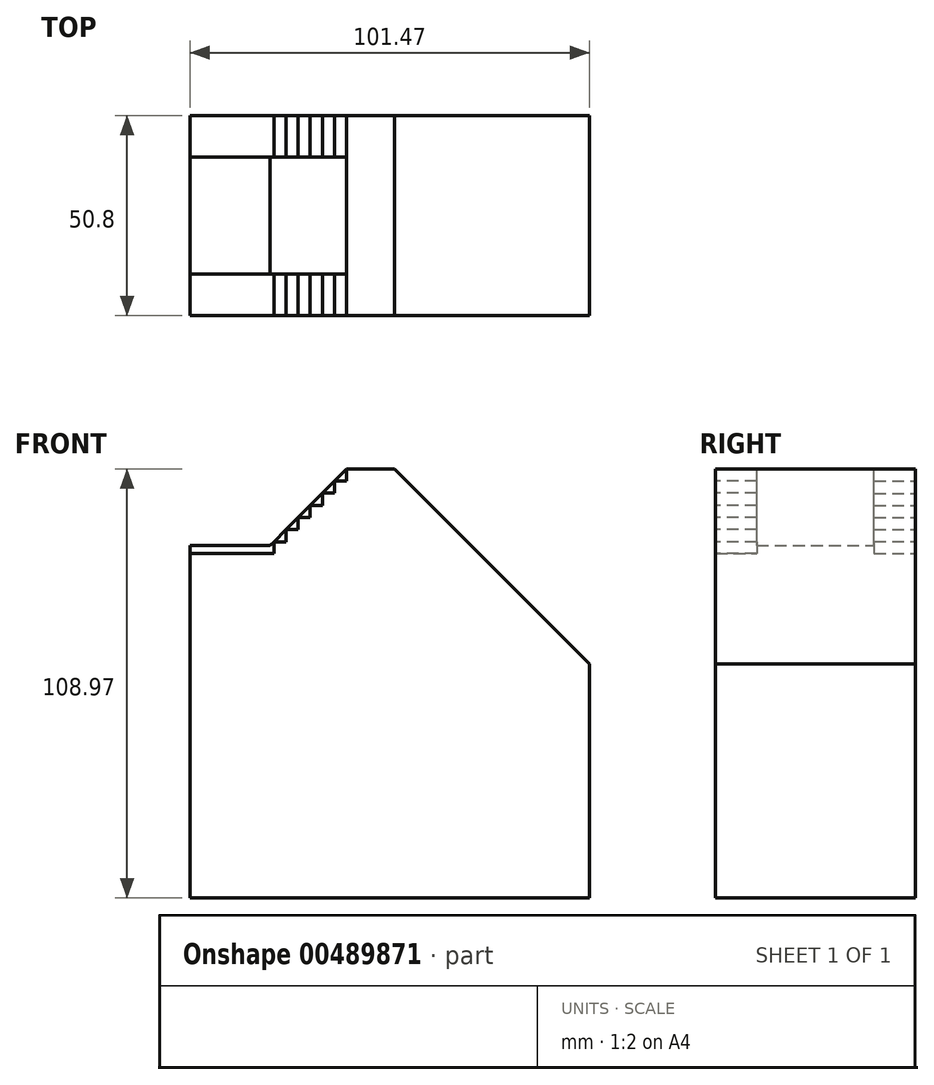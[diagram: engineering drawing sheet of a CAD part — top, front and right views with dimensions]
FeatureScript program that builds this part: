
annotation { "Feature Type Name" : "Feature", "Feature Type Description" : "" }
export const myFeature = defineFeature(function(context is Context, id is Id, definition is map)
    precondition{}
    {
        {
            var Q0;
            Q0=qCreatedBy(makeId("Front.planeOp"),FACE);
            var sketch = newSketch(context, id + "F0", { "sketchPlane" : qUnion([Q0])});
            skLineSegment(sketch, "E0", {"start": v(0, 0) * mm, "end": v(0, 87.48) * mm});
            skLineSegment(sketch, "E1", {"start": v(0, 87.48) * mm, "end": v(18.26, 87.48) * mm});
            skLineSegment(sketch, "E2", {"start": v(18.26, 87.48) * mm, "end": v(39.75, 108.97) * mm});
            skLineSegment(sketch, "E3", {"start": v(39.75, 108.97) * mm, "end": v(52, 108.97) * mm});
            skLineSegment(sketch, "E4", {"start": v(52, 108.97) * mm, "end": v(101.47, 59.49) * mm});
            skLineSegment(sketch, "E5", {"start": v(101.47, 59.49) * mm, "end": v(101.47, 0) * mm});
            skLineSegment(sketch, "E6", {"start": v(101.47, 0) * mm, "end": v(0, 0) * mm});
            skSolve(sketch);
        }
        {
            var Q0;
            Q0 = qSketchRegion(id + "F0", true);
            extrude(context, id + "F1", {"entities" : qUnion([Q0]), "depth" : 50.8 * mm});
        }
        {
            var Q0;
            Q0=makeQuery(id+"F1.opExtrude","CAP_FACE",FACE,{"disambiguationData":[OSD([sQuery(id+"F0.wireOp",EDGE,"E0"),sQuery(id+"F0.wireOp",EDGE,"E1"),sQuery(id+"F0.wireOp",EDGE,"E2"),sQuery(id+"F0.wireOp",EDGE,"E3"),sQuery(id+"F0.wireOp",EDGE,"E4"),sQuery(id+"F0.wireOp",EDGE,"E5"),sQuery(id+"F0.wireOp",EDGE,"E6")])],"isStart":false});
            var sketch = newSketch(context, id + "F2", { "sketchPlane" : qUnion([Q0])});
            skLineSegment(sketch, "E7", {"start": v(39.75, 108.97) * mm, "end": v(39.75, 105.9) * mm});
            skLineSegment(sketch, "E8", {"start": v(39.75, 105.9) * mm, "end": v(36.68, 105.9) * mm});
            skLineSegment(sketch, "E9", {"start": v(36.68, 105.9) * mm, "end": v(36.68, 102.82) * mm});
            skLineSegment(sketch, "E10", {"start": v(36.68, 102.82) * mm, "end": v(33.6, 102.82) * mm});
            skLineSegment(sketch, "E11", {"start": v(33.6, 102.82) * mm, "end": v(33.6, 99.74) * mm});
            skLineSegment(sketch, "E12", {"start": v(33.6, 99.74) * mm, "end": v(30.52, 99.74) * mm});
            skLineSegment(sketch, "E13", {"start": v(30.52, 99.74) * mm, "end": v(30.52, 96.66) * mm});
            skLineSegment(sketch, "E14", {"start": v(30.52, 96.66) * mm, "end": v(27.44, 96.66) * mm});
            skLineSegment(sketch, "E15", {"start": v(27.44, 96.66) * mm, "end": v(27.44, 93.58) * mm});
            skLineSegment(sketch, "E16", {"start": v(27.44, 93.58) * mm, "end": v(24.36, 93.58) * mm});
            skLineSegment(sketch, "E17", {"start": v(24.36, 93.58) * mm, "end": v(24.36, 90.5) * mm});
            skLineSegment(sketch, "E18", {"start": v(24.36, 90.5) * mm, "end": v(21.28, 90.5) * mm});
            skLineSegment(sketch, "E19", {"start": v(21.28, 90.5) * mm, "end": v(21.28, 87.48) * mm});
            skLineSegment(sketch, "E20", {"start": v(21.28, 87.48) * mm, "end": v(18.26, 87.48) * mm});
            skLineSegment(sketch, "E21", {"start": v(18.26, 87.48) * mm, "end": v(39.75, 108.97) * mm});
            skSolve(sketch);
        }
        {
            var Q0;
            Q0 = qSketchRegion(id + "F2", true);
            extrude(context, id + "F3", {"entities" : qUnion([Q0]), "operationType" : NewBodyOperationType.REMOVE, "oppositeDirection" : true, "depth" : 10.5 * mm});
        }
        {
            var Q0;
            Q0=makeQuery(id+"F1.opExtrude","CAP_FACE",FACE,{"disambiguationData":[OSD([sQuery(id+"F0.wireOp",EDGE,"E0"),sQuery(id+"F0.wireOp",EDGE,"E1"),sQuery(id+"F0.wireOp",EDGE,"E2"),sQuery(id+"F0.wireOp",EDGE,"E3"),sQuery(id+"F0.wireOp",EDGE,"E4"),sQuery(id+"F0.wireOp",EDGE,"E5"),sQuery(id+"F0.wireOp",EDGE,"E6")])],"isStart":true});
            var sketch = newSketch(context, id + "F4", { "sketchPlane" : qUnion([Q0])});
            skLineSegment(sketch, "E22", {"start": v(-39.75, 108.97) * mm, "end": v(-39.75, 105.9) * mm});
            skLineSegment(sketch, "E23", {"start": v(-39.75, 105.9) * mm, "end": v(-36.67, 105.9) * mm});
            skLineSegment(sketch, "E24", {"start": v(-36.67, 105.9) * mm, "end": v(-36.67, 102.81) * mm});
            skLineSegment(sketch, "E25", {"start": v(-36.67, 102.81) * mm, "end": v(-33.6, 102.81) * mm});
            skLineSegment(sketch, "E26", {"start": v(-33.6, 102.81) * mm, "end": v(-33.6, 99.74) * mm});
            skLineSegment(sketch, "E27", {"start": v(-33.6, 99.74) * mm, "end": v(-30.52, 99.74) * mm});
            skLineSegment(sketch, "E28", {"start": v(-30.52, 99.74) * mm, "end": v(-30.52, 96.66) * mm});
            skLineSegment(sketch, "E29", {"start": v(-30.52, 96.66) * mm, "end": v(-27.44, 96.66) * mm});
            skLineSegment(sketch, "E30", {"start": v(-27.44, 96.66) * mm, "end": v(-27.44, 93.58) * mm});
            skLineSegment(sketch, "E31", {"start": v(-27.44, 93.58) * mm, "end": v(-24.36, 93.58) * mm});
            skLineSegment(sketch, "E32", {"start": v(-24.36, 93.58) * mm, "end": v(-24.36, 90.5) * mm});
            skLineSegment(sketch, "E33", {"start": v(-24.36, 90.5) * mm, "end": v(-21.28, 90.5) * mm});
            skLineSegment(sketch, "E34", {"start": v(-21.28, 90.5) * mm, "end": v(-21.28, 87.48) * mm});
            skLineSegment(sketch, "E35", {"start": v(-21.28, 87.48) * mm, "end": v(-18.26, 87.48) * mm});
            skLineSegment(sketch, "E36", {"start": v(-39.75, 108.97) * mm, "end": v(-18.26, 87.48) * mm});
            skSolve(sketch);
        }
        {
            var Q0;
            Q0 = qSketchRegion(id + "F4", true);
            extrude(context, id + "F5", {"entities" : qUnion([Q0]), "operationType" : NewBodyOperationType.REMOVE, "oppositeDirection" : true, "depth" : 10.5 * mm});
        }
        {
            var Q0;
            Q0=makeQuery(id+"F5.boolean.opBoolean","MERGE",FACE,{"derivedFrom":[makeQuery(id+"F1.opExtrude","SWEPT_FACE",FACE,{"disambiguationData":[OSD([sQuery(id+"F0.wireOp",EDGE,"E1")])]}),makeQuery(id+"F5.opExtrude","SWEPT_FACE",FACE,{"disambiguationData":[OSD([sQuery(id+"F4.wireOp",EDGE,"E35")])]})]});
            var sketch = newSketch(context, id + "F6", { "sketchPlane" : qUnion([Q0])});
            skLineSegment(sketch, "E37", {"start": v(0, -40.3) * mm, "end": v(0, -10.5) * mm});
            skLineSegment(sketch, "E38", {"start": v(0, -40.3) * mm, "end": v(24.44, -40.3) * mm});
            skLineSegment(sketch, "E39", {"start": v(24.44, -40.3) * mm, "end": v(24.44, -10.5) * mm});
            skLineSegment(sketch, "E40", {"start": v(24.44, -10.5) * mm, "end": v(0, -10.5) * mm});
            skSolve(sketch);
        }
        {
            var Q0;
            Q0 = qSketchRegion(id + "F6", true);
            extrude(context, id + "F7", {"entities" : qUnion([Q0]), "operationType" : NewBodyOperationType.ADD, "depth" : 2.03 * mm});
        }
    });
